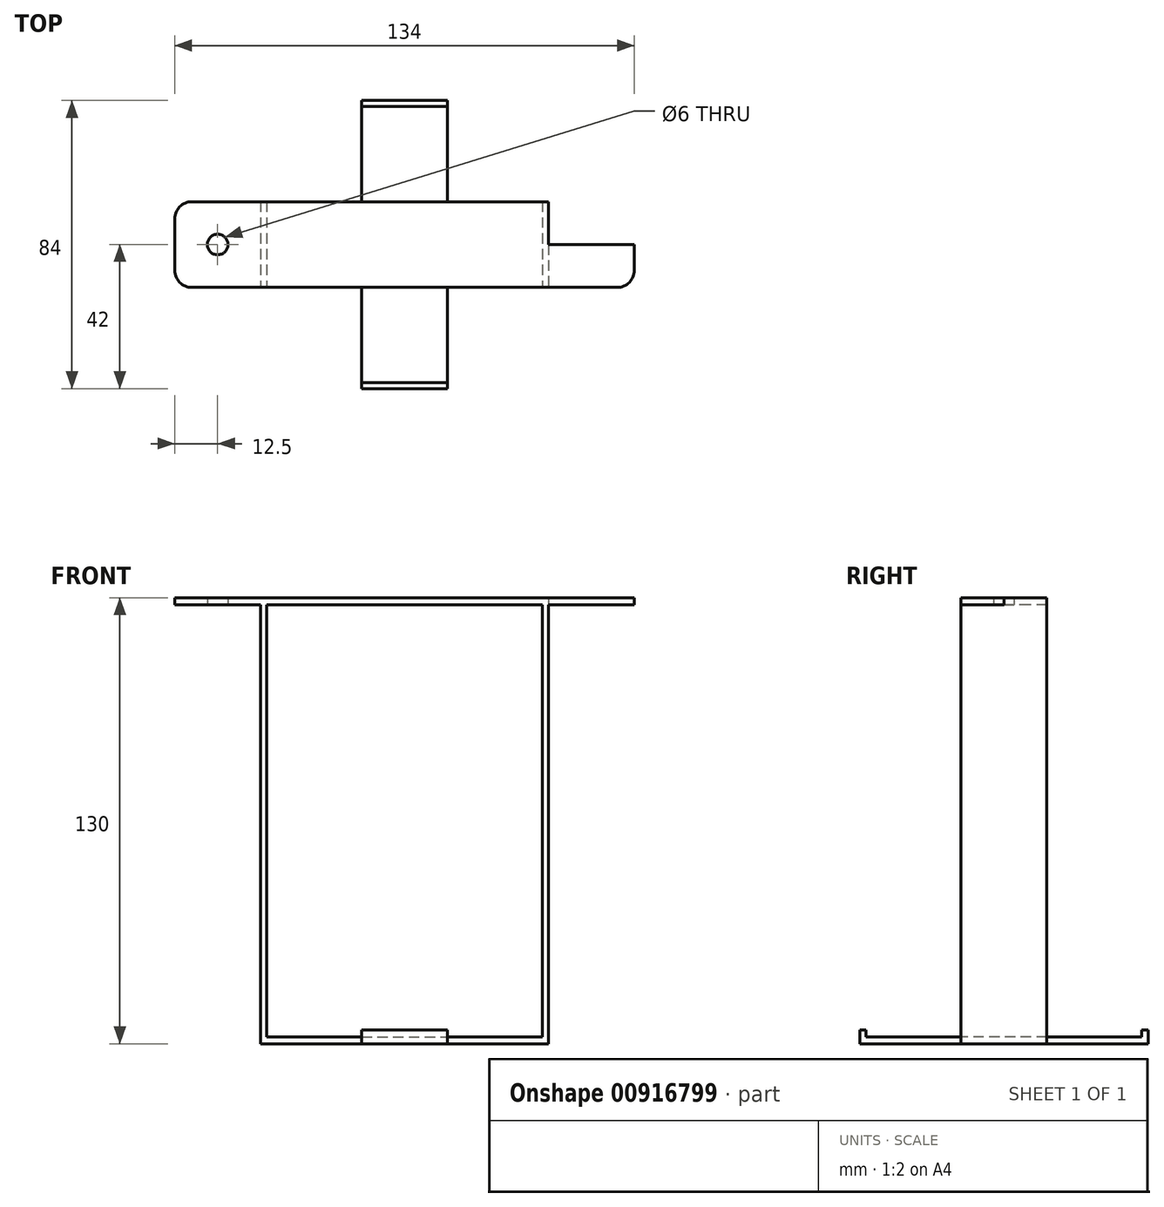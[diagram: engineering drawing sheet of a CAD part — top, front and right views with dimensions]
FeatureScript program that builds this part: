
annotation { "Feature Type Name" : "Feature", "Feature Type Description" : "" }
export const myFeature = defineFeature(function(context is Context, id is Id, definition is map)
    precondition{}
    {
        {
            var Q0;
            Q0=qCreatedBy(makeId("Top.planeOp"),FACE);
            var sketch = newSketch(context, id + "F0", { "sketchPlane" : qUnion([Q0])});
            skLineSegment(sketch, "E0.bottom", {"start": v(42, 12.5) * mm, "end": v(-42, 12.5) * mm});
            skLineSegment(sketch, "E0.top", {"start": v(42, -12.5) * mm, "end": v(-42, -12.5) * mm});
            skLineSegment(sketch, "E0.left", {"start": v(42, 12.5) * mm, "end": v(42, -12.5) * mm});
            skLineSegment(sketch, "E0.right", {"start": v(-42, 12.5) * mm, "end": v(-42, -12.5) * mm});
            skPoint(sketch, "E0.middle", {"position": v(0, 0) * mm});
            skLineSegment(sketch, "E1.bottom", {"start": v(12.5, 42) * mm, "end": v(-12.5, 42) * mm});
            skLineSegment(sketch, "E1.top", {"start": v(12.5, -42) * mm, "end": v(-12.5, -42) * mm});
            skLineSegment(sketch, "E1.left", {"start": v(12.5, 42) * mm, "end": v(12.5, -42) * mm});
            skLineSegment(sketch, "E1.right", {"start": v(-12.5, 42) * mm, "end": v(-12.5, -42) * mm});
            skLineSegment(sketch, "E2", {"start": v(-12.5, 40.2) * mm, "end": v(12.5, 40.2) * mm});
            skLineSegment(sketch, "E3", {"start": v(-40.2, 12.5) * mm, "end": v(-40.2, -12.5) * mm});
            skLineSegment(sketch, "E4", {"start": v(40.2, 12.5) * mm, "end": v(40.2, -12.5) * mm});
            skLineSegment(sketch, "E5", {"start": v(-12.5, -40.2) * mm, "end": v(12.5, -40.2) * mm});
            skSolve(sketch);
        }
        {
            var Q0;
            {var subQ5=sQuery(id+"F0.wireOp",EDGE,"E2");Q0=makeQuery(id+"F0.imprint","IMPRINT",FACE,{"disambiguationData":[TD([[makeQuery(id+"F0.imprint","IMPRINT",EDGE,{"derivedFrom":subQ5}),-1.0]])]});}
            var Q1;
            {var subQ0=sQuery(id+"F0.wireOp",EDGE,"E1.left");var subQ1=sQuery(id+"F0.wireOp",EDGE,"E0.bottom");var subQ2=makeQuery(id+"F0.imprint","INTERSECT",VERTEX,{"derivedFrom":[subQ1,subQ0]});Q1=makeQuery(id+"F0.imprint","IMPRINT",FACE,{"disambiguationData":[TD([[makeQuery(id+"F0.imprint","IMPRINT",EDGE,{"disambiguationData":[TD([[subQ2,-1.0]])],"derivedFrom":subQ1}),1.0]])]});}
            var Q2;
            {var subQ0=sQuery(id+"F0.wireOp",EDGE,"E4");Q2=makeQuery(id+"F0.imprint","IMPRINT",FACE,{"disambiguationData":[TD([[makeQuery(id+"F0.imprint","IMPRINT",EDGE,{"derivedFrom":subQ0}),-1.0]])]});}
            var Q3;
            {var subQ5=sQuery(id+"F0.wireOp",EDGE,"E5");Q3=makeQuery(id+"F0.imprint","IMPRINT",FACE,{"disambiguationData":[TD([[makeQuery(id+"F0.imprint","IMPRINT",EDGE,{"derivedFrom":subQ5}),1.0]])]});}
            var Q4;
            {var subQ0=sQuery(id+"F0.wireOp",EDGE,"E3");Q4=makeQuery(id+"F0.imprint","IMPRINT",FACE,{"disambiguationData":[TD([[makeQuery(id+"F0.imprint","IMPRINT",EDGE,{"derivedFrom":subQ0}),1.0]])]});}
            extrude(context, id + "F1", {"entities" : qUnion([Q0, Q1, Q2, Q3, Q4]), "depth" : 2 * mm, "offsetDistance" : 25 * mm});
        }
        {
            var Q0;
            {var subQ0=sQuery(id+"F0.wireOp",EDGE,"E0.right");Q0=makeQuery(id+"F0.imprint","IMPRINT",FACE,{"disambiguationData":[TD([[makeQuery(id+"F0.imprint","IMPRINT",EDGE,{"derivedFrom":subQ0}),1.0]])]});}
            var Q1;
            {var subQ0=sQuery(id+"F0.wireOp",EDGE,"E0.left");Q1=makeQuery(id+"F0.imprint","IMPRINT",FACE,{"disambiguationData":[TD([[makeQuery(id+"F0.imprint","IMPRINT",EDGE,{"derivedFrom":subQ0}),-1.0]])]});}
            extrude(context, id + "F2", {"entities" : qUnion([Q0, Q1]), "operationType" : NewBodyOperationType.ADD, "depth" : 130 * mm, "offsetDistance" : 25 * mm});
        }
        {
            var Q0;
            {var subQ0=sQuery(id+"F0.wireOp",EDGE,"E1.bottom");Q0=makeQuery(id+"F0.imprint","IMPRINT",FACE,{"disambiguationData":[TD([[makeQuery(id+"F0.imprint","IMPRINT",EDGE,{"derivedFrom":subQ0}),1.0]])]});}
            var Q1;
            {var subQ0=sQuery(id+"F0.wireOp",EDGE,"E1.top");Q1=makeQuery(id+"F0.imprint","IMPRINT",FACE,{"disambiguationData":[TD([[makeQuery(id+"F0.imprint","IMPRINT",EDGE,{"derivedFrom":subQ0}),-1.0]])]});}
            extrude(context, id + "F3", {"entities" : qUnion([Q0, Q1]), "operationType" : NewBodyOperationType.ADD, "depth" : 4 * mm, "offsetDistance" : 25 * mm});
        }
        {
            var Q0;
            Q0=makeQuery(id+"F2.opExtrude","SWEPT_FACE",FACE,{"disambiguationData":[OSD([sQuery(id+"F0.wireOp",EDGE,"E4")])]});
            var sketch = newSketch(context, id + "F4", { "sketchPlane" : qUnion([Q0])});
            skLineSegment(sketch, "E6", {"start": v(-12.5, 128) * mm, "end": v(12.5, 128) * mm});
            skSolve(sketch);
        }
        {
            var Q0;
            Q0 = qSketchRegion(id + "F4", true);
            var Q1;
            {var subQ0=sQuery(id+"F4.wireOp",EDGE,"E6");Q1=makeQuery(id+"F4.imprint","IMPRINT",FACE,{"disambiguationData":[TD([[makeQuery(id+"F4.imprint","IMPRINT",EDGE,{"derivedFrom":subQ0}),1.0]])]});}
            extrude(context, id + "F5", {"entities" : qUnion([Q0, Q1]), "operationType" : NewBodyOperationType.ADD, "depth" : 80.4 * mm, "offsetDistance" : 25 * mm});
        }
        {
            var Q0;
            Q0=makeQuery(id+"F2.opExtrude","SWEPT_FACE",FACE,{"disambiguationData":[OSD([sQuery(id+"F0.wireOp",EDGE,"E0.right")])]});
            var sketch = newSketch(context, id + "F6", { "sketchPlane" : qUnion([Q0])});
            skLineSegment(sketch, "E7", {"start": v(-12.5, 128) * mm, "end": v(12.5, 128) * mm});
            skSolve(sketch);
        }
        {
            var Q0;
            Q0=makeQuery(id+"F2.opExtrude","SWEPT_FACE",FACE,{"disambiguationData":[OSD([sQuery(id+"F0.wireOp",EDGE,"E0.left")])]});
            var sketch = newSketch(context, id + "F7", { "sketchPlane" : qUnion([Q0])});
            skLineSegment(sketch, "E8", {"start": v(12.5, 128) * mm, "end": v(-12.5, 128) * mm});
            skSolve(sketch);
        }
        {
            var Q0;
            {var subQ0=sQuery(id+"F7.wireOp",EDGE,"E8");Q0=makeQuery(id+"F7.imprint","IMPRINT",FACE,{"disambiguationData":[TD([[makeQuery(id+"F7.imprint","IMPRINT",EDGE,{"derivedFrom":subQ0}),-1.0]])]});}
            extrude(context, id + "F8", {"entities" : qUnion([Q0]), "operationType" : NewBodyOperationType.ADD, "depth" : 25 * mm, "offsetDistance" : 25 * mm});
        }
        {
            var Q0;
            {var subQ0=sQuery(id+"F6.wireOp",EDGE,"E7");Q0=makeQuery(id+"F6.imprint","IMPRINT",FACE,{"disambiguationData":[TD([[makeQuery(id+"F6.imprint","IMPRINT",EDGE,{"derivedFrom":subQ0}),1.0]])]});}
            extrude(context, id + "F9", {"entities" : qUnion([Q0]), "operationType" : NewBodyOperationType.ADD, "depth" : 25 * mm, "offsetDistance" : 25 * mm});
        }
        {
            var Q0;
            Q0=makeQuery(id+"F8.opExtrude","SWEPT_FACE",FACE,{"disambiguationData":[OSD([sQuery(id+"F7.wireOp",EDGE,"E8")])]});
            var sketch = newSketch(context, id + "F10", { "sketchPlane" : qUnion([Q0])});
            skLineSegment(sketch, "E9", {"start": v(54.5, 12.5) * mm, "end": v(54.5, -12.5) * mm});
            skLineSegment(sketch, "E10", {"start": v(67, 0) * mm, "end": v(42, 0) * mm});
            skCircle(sketch, "E11", {"center": v(54.5, 0) * mm, "radius": 3 * mm});
            skSolve(sketch);
        }
        {
            var Q0;
            Q0=makeQuery(id+"F9.opExtrude","SWEPT_FACE",FACE,{"disambiguationData":[OSD([sQuery(id+"F6.wireOp",EDGE,"E7")])]});
            var sketch = newSketch(context, id + "F11", { "sketchPlane" : qUnion([Q0])});
            skLineSegment(sketch, "E12", {"start": v(-54.5, 12.5) * mm, "end": v(-54.5, -12.5) * mm});
            skLineSegment(sketch, "E13", {"start": v(-67, 0) * mm, "end": v(-42, 0) * mm});
            skCircle(sketch, "E14", {"center": v(-54.5, 0) * mm, "radius": 3 * mm});
            skSolve(sketch);
        }
        {
            var Q0;
            {var subQ0=sQuery(id+"F11.wireOp",EDGE,"E14");var subQ1=sQuery(id+"F11.wireOp",EDGE,"E12");var subQ2=makeQuery(id+"F11.imprint","INTERSECT",VERTEX,{"disambiguationData":[OD(0.0)],"derivedFrom":[subQ1,subQ0]});Q0=makeQuery(id+"F11.imprint","IMPRINT",FACE,{"disambiguationData":[TD([[makeQuery(id+"F11.imprint","IMPRINT",EDGE,{"disambiguationData":[TD([[subQ2,-1.0]])],"derivedFrom":subQ1}),1.0]])]});}
            var Q1;
            {var subQ0=sQuery(id+"F11.wireOp",EDGE,"E14");var subQ1=sQuery(id+"F11.wireOp",EDGE,"E12");var subQ2=makeQuery(id+"F11.imprint","INTERSECT",VERTEX,{"disambiguationData":[OD(0.0)],"derivedFrom":[subQ1,subQ0]});Q1=makeQuery(id+"F11.imprint","IMPRINT",FACE,{"disambiguationData":[TD([[makeQuery(id+"F11.imprint","IMPRINT",EDGE,{"disambiguationData":[TD([[subQ2,-1.0]])],"derivedFrom":subQ1}),-1.0]])]});}
            var Q2;
            {var subQ0=sQuery(id+"F11.wireOp",EDGE,"E13");var subQ1=sQuery(id+"F11.wireOp",EDGE,"E12");var subQ2=makeQuery(id+"F11.imprint","INTERSECT",VERTEX,{"derivedFrom":[subQ1,subQ0]});Q2=makeQuery(id+"F11.imprint","IMPRINT",FACE,{"disambiguationData":[TD([[makeQuery(id+"F11.imprint","IMPRINT",EDGE,{"disambiguationData":[TD([[subQ2,-1.0]])],"derivedFrom":subQ1}),1.0]])]});}
            var Q3;
            {var subQ0=sQuery(id+"F11.wireOp",EDGE,"E13");var subQ1=sQuery(id+"F11.wireOp",EDGE,"E12");var subQ2=makeQuery(id+"F11.imprint","INTERSECT",VERTEX,{"derivedFrom":[subQ1,subQ0]});Q3=makeQuery(id+"F11.imprint","IMPRINT",FACE,{"disambiguationData":[TD([[makeQuery(id+"F11.imprint","IMPRINT",EDGE,{"disambiguationData":[TD([[subQ2,-1.0]])],"derivedFrom":subQ1}),-1.0]])]});}
            var Q4;
            {var subQ0=sQuery(id+"F10.wireOp",EDGE,"E11");var subQ1=sQuery(id+"F10.wireOp",EDGE,"E9");var subQ2=makeQuery(id+"F10.imprint","INTERSECT",VERTEX,{"disambiguationData":[OD(0.0)],"derivedFrom":[subQ1,subQ0]});Q4=makeQuery(id+"F10.imprint","IMPRINT",FACE,{"disambiguationData":[TD([[makeQuery(id+"F10.imprint","IMPRINT",EDGE,{"disambiguationData":[TD([[subQ2,-1.0]])],"derivedFrom":subQ1}),-1.0]])]});}
            var Q5;
            {var subQ0=sQuery(id+"F10.wireOp",EDGE,"E11");var subQ1=sQuery(id+"F10.wireOp",EDGE,"E9");var subQ2=makeQuery(id+"F10.imprint","INTERSECT",VERTEX,{"disambiguationData":[OD(0.0)],"derivedFrom":[subQ1,subQ0]});Q5=makeQuery(id+"F10.imprint","IMPRINT",FACE,{"disambiguationData":[TD([[makeQuery(id+"F10.imprint","IMPRINT",EDGE,{"disambiguationData":[TD([[subQ2,-1.0]])],"derivedFrom":subQ1}),1.0]])]});}
            var Q6;
            {var subQ0=sQuery(id+"F10.wireOp",EDGE,"E10");var subQ1=sQuery(id+"F10.wireOp",EDGE,"E9");var subQ2=makeQuery(id+"F10.imprint","INTERSECT",VERTEX,{"derivedFrom":[subQ1,subQ0]});Q6=makeQuery(id+"F10.imprint","IMPRINT",FACE,{"disambiguationData":[TD([[makeQuery(id+"F10.imprint","IMPRINT",EDGE,{"disambiguationData":[TD([[subQ2,-1.0]])],"derivedFrom":subQ1}),1.0]])]});}
            var Q7;
            {var subQ0=sQuery(id+"F10.wireOp",EDGE,"E10");var subQ1=sQuery(id+"F10.wireOp",EDGE,"E9");var subQ2=makeQuery(id+"F10.imprint","INTERSECT",VERTEX,{"derivedFrom":[subQ1,subQ0]});Q7=makeQuery(id+"F10.imprint","IMPRINT",FACE,{"disambiguationData":[TD([[makeQuery(id+"F10.imprint","IMPRINT",EDGE,{"disambiguationData":[TD([[subQ2,-1.0]])],"derivedFrom":subQ1}),-1.0]])]});}
            extrude(context, id + "F12", {"entities" : qUnion([Q0, Q1, Q2, Q3, Q4, Q5, Q6, Q7]), "operationType" : NewBodyOperationType.REMOVE, "oppositeDirection" : true, "depth" : 25 * mm, "offsetDistance" : 25 * mm});
        }
        {
            var Q0;
            Q0=makeQuery(id+"F8.opExtrude","CAP_EDGE",EDGE,{"disambiguationData":[OSD([sQuery(id+"F0.wireOp",EDGE,"E0.bottom"),sQuery(id+"F0.wireOp",EDGE,"E0.left")])],"isStart":false});
            var Q1;
            Q1=makeQuery(id+"F8.opExtrude","CAP_EDGE",EDGE,{"disambiguationData":[OSD([sQuery(id+"F0.wireOp",EDGE,"E0.top"),sQuery(id+"F0.wireOp",EDGE,"E0.left")])],"isStart":false});
            var Q2;
            Q2=makeQuery(id+"F9.opExtrude","CAP_EDGE",EDGE,{"disambiguationData":[OSD([sQuery(id+"F0.wireOp",EDGE,"E0.bottom"),sQuery(id+"F0.wireOp",EDGE,"E0.right")])],"isStart":false});
            var Q3;
            Q3=makeQuery(id+"F9.opExtrude","CAP_EDGE",EDGE,{"disambiguationData":[OSD([sQuery(id+"F0.wireOp",EDGE,"E0.top"),sQuery(id+"F0.wireOp",EDGE,"E0.right")])],"isStart":false});
            fillet(context, id + "F13", {"entities" : qUnion([Q0, Q1, Q2, Q3]), "radius" : 5 * mm, "tangentPropagation" : true, "allowEdgeOverflow" : false});
        }
    });
